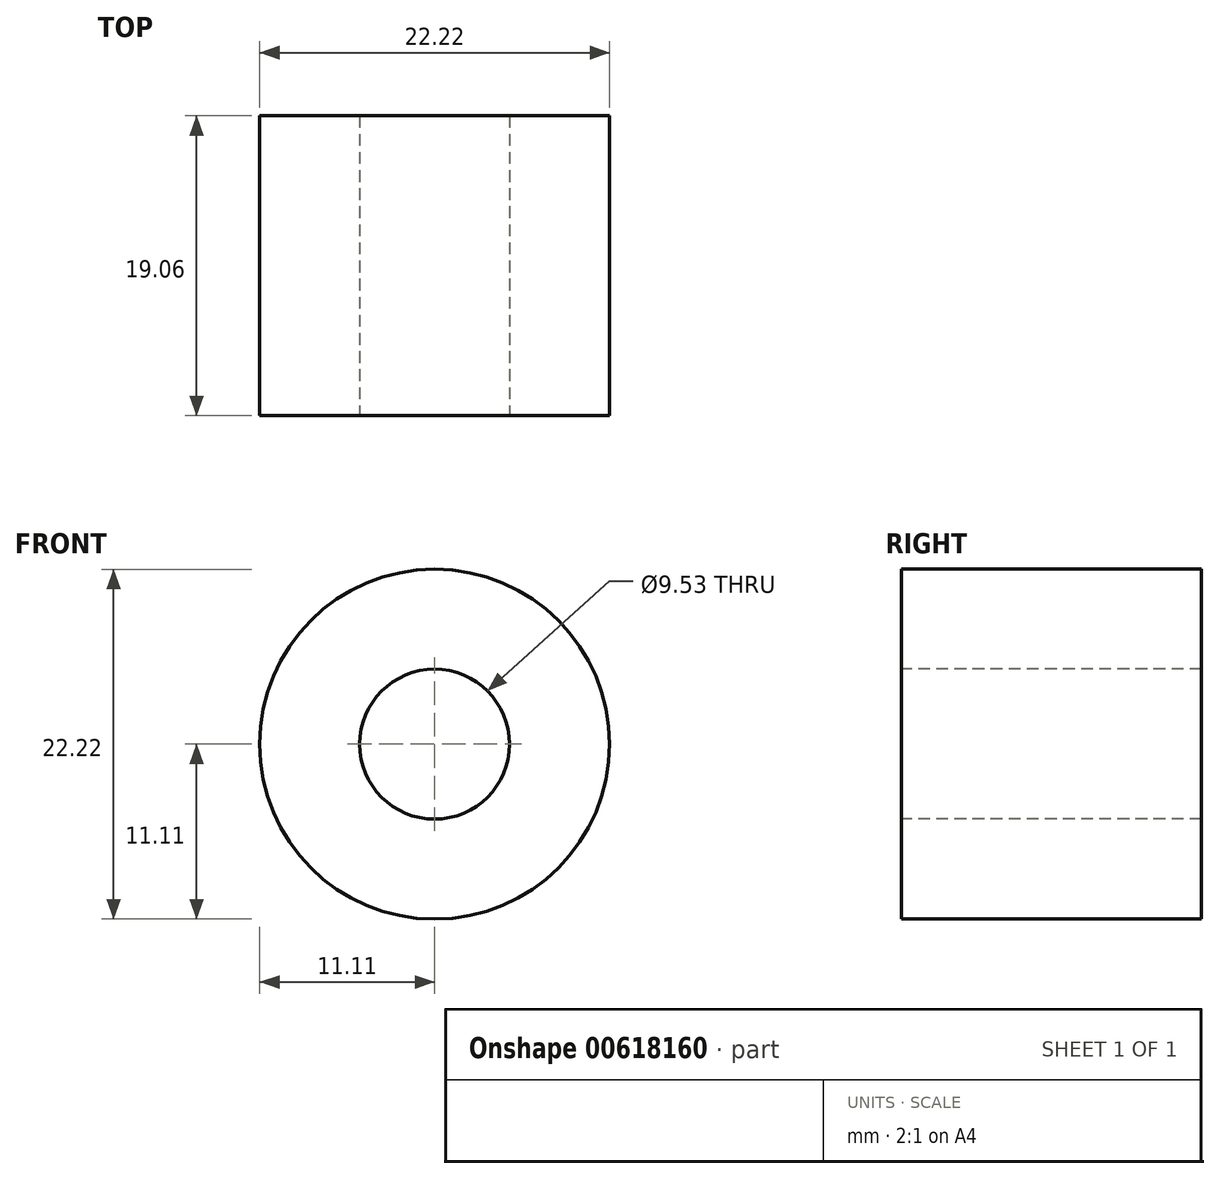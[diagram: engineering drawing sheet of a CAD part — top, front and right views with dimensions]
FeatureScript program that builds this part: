
annotation { "Feature Type Name" : "Feature", "Feature Type Description" : "" }
export const myFeature = defineFeature(function(context is Context, id is Id, definition is map)
    precondition{}
    {
        {
            var Q0;
            Q0=qCreatedBy(makeId("Top.planeOp"),FACE);
            var sketch = newSketch(context, id + "F0", { "sketchPlane" : qUnion([Q0])});
            skLineSegment(sketch, "E0", {"start": v(-4.76, 9.52) * mm, "end": v(-4.76, -9.53) * mm});
            skLineSegment(sketch, "E1", {"start": v(-4.76, 9.52) * mm, "end": v(-11.11, 9.52) * mm});
            skLineSegment(sketch, "E2", {"start": v(-11.11, 9.52) * mm, "end": v(-11.11, -9.53) * mm});
            skLineSegment(sketch, "E3", {"start": v(-11.11, -9.53) * mm, "end": v(-4.76, -9.53) * mm});
            skLineSegment(sketch, "E4", {"start": v(0, 0) * mm, "end": v(0, 14.35) * mm, "construction": true});
            skSolve(sketch);
        }
        {
            var Q0;
            Q0=qSketchRegion(id+"F0",true);
            var Q1;
            Q1=sQuery(id+"F0.wireOp",EDGE,"E4");
            revolve(context, id + "F1", {"entities" : qUnion([Q0]), "axis" : qUnion([Q1]), "revolveType" : RevolveType.FULL});
        }
    });
